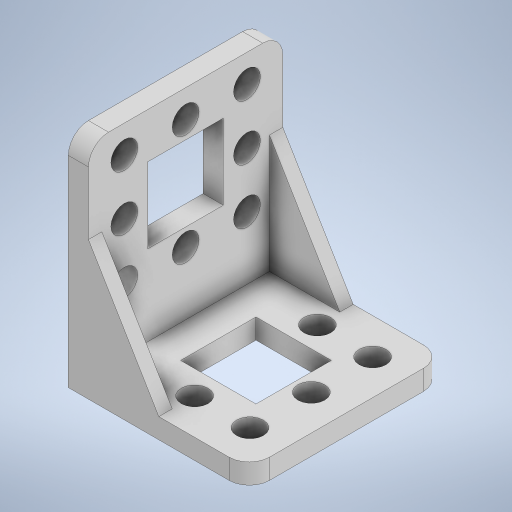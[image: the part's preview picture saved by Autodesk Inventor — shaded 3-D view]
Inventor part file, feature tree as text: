
AUTODESK INVENTOR PART (.ipt)
format: ipt  version: 2023.1 (Build 271208000, 208)  size: 351,232 bytes
history: native  units: mm
features: extrude x4, sketch x4, fillet x2
ambient origin geometry x8: Origin, YZ Plane, XZ Plane, XY Plane, X Axis, Y Axis, Z Axis, Center Point
bodies: Solid1 (feature_tree)
feature tree (10):
  extrude  "Extrusion1"  Depth=27.0mm
  fillet  "Fillet1"  Radius=13.5mm
  extrude  "Extrusion2"  Depth=11.25mm
  fillet  "Fillet2"  Radius=11.25mm
  extrude  "Extrusion3"  Depth=5.625mm
  extrude  "Extrusion4"  Depth=2.0mm
  sketch  "Sketch1"  dims[d0=29.0mm d1=27.0mm d2=13.5mm]
  sketch  "Sketch2"  dims[d3=14.5mm d4=11.25mm d5=11.25mm]
  sketch  "Sketch3"  dims[d6=5.625mm d7=5.625mm]
  sketch  "Sketch4"  dims[d8=4.0mm d9=5.25mm d10=4.0mm d12=5.35mm d13=4.125mm d14=3.0mm d15=0.0mm d16=3.0mm d17=29.0mm d18=33.0mm d19=11.25mm d20=11.25mm d21=12.0mm d22=8.875mm d23=2.625mm d24=4.0mm d25=2.625mm d26=4.0mm d27=5.35mm d28=0.0mm d29=5.625mm d30=5.625mm d31=8.25mm d32=4.125mm d33=3.0mm d34=0.0mm d35=3.0mm d36=2.0mm d37=0.0mm d38=2.0mm d39=0.0mm]
